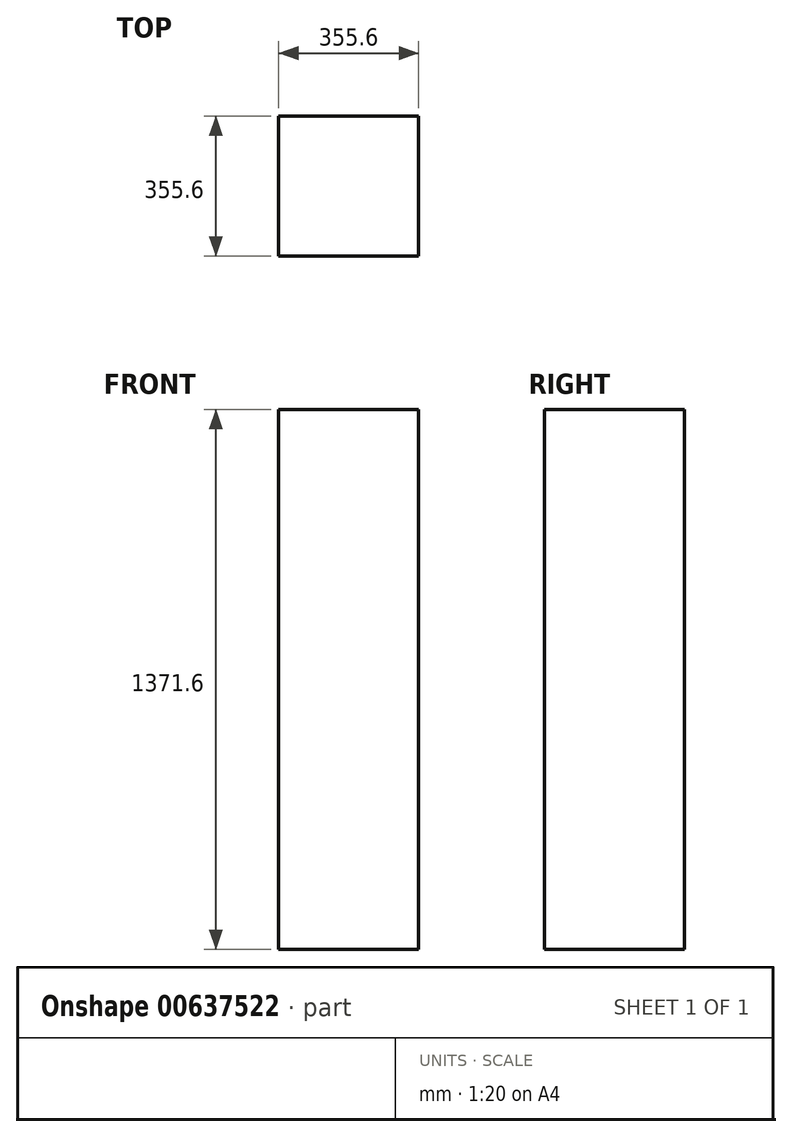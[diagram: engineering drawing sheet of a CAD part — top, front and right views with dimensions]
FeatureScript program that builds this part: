
annotation { "Feature Type Name" : "Feature", "Feature Type Description" : "" }
export const myFeature = defineFeature(function(context is Context, id is Id, definition is map)
    precondition{}
    {
        {
            var Q0;
            Q0=qCreatedBy(makeId("Top.planeOp"),FACE);
            var sketch = newSketch(context, id + "F0", { "sketchPlane" : qUnion([Q0])});
            skLineSegment(sketch, "E0.bottom", {"start": v(0, 0) * mm, "end": v(355.6, 0) * mm});
            skLineSegment(sketch, "E0.top", {"start": v(0, 355.6) * mm, "end": v(355.6, 355.6) * mm});
            skLineSegment(sketch, "E0.left", {"start": v(0, 0) * mm, "end": v(0, 355.6) * mm});
            skLineSegment(sketch, "E0.right", {"start": v(355.6, 0) * mm, "end": v(355.6, 355.6) * mm});
            skSolve(sketch);
        }
        {
            var Q0;
            Q0=qSketchRegion(id+"F0",true);
            extrude(context, id + "F1", {"entities" : qUnion([Q0]), "depth" : 1371.6 * mm});
        }
    });
